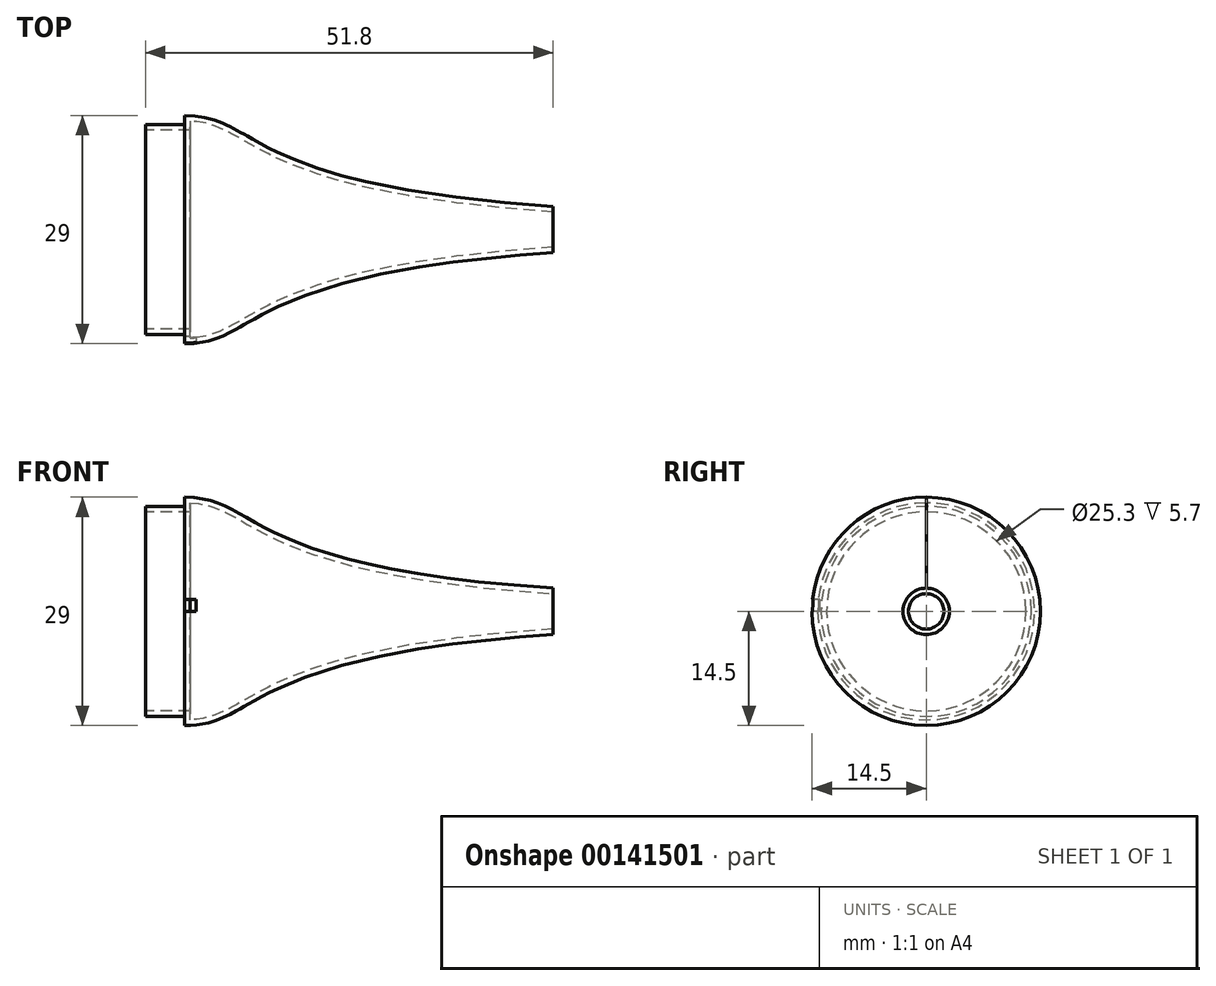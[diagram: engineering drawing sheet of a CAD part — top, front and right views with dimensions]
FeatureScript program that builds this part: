
annotation { "Feature Type Name" : "Feature", "Feature Type Description" : "" }
export const myFeature = defineFeature(function(context is Context, id is Id, definition is map)
    precondition{}
    {
        {
            var Q0;
            Q0=qCreatedBy(makeId("Front.planeOp"),FACE);
            var sketch = newSketch(context, id + "F0", { "sketchPlane" : qUnion([Q0])});
            skLineSegment(sketch, "E0", {"start": v(-28.81, 0) * mm, "end": v(31.47, 0) * mm, "construction": true});
            skLineSegment(sketch, "E1", {"start": v(0, 0) * mm, "end": v(0, 13.35) * mm});
            skLineSegment(sketch, "E2", {"start": v(0, 13.35) * mm, "end": v(5, 13.35) * mm});
            skLineSegment(sketch, "E3", {"start": v(5, 13.35) * mm, "end": v(5, 14.5) * mm});
            skLineSegment(sketch, "E4", {"start": v(51.8, 2.95) * mm, "end": v(51.8, 0) * mm});
            skLineSegment(sketch, "E5", {"start": v(51.8, 0) * mm, "end": v(0, 0) * mm});
            skFitSpline(sketch, "E6", {"points": [v(5, 14.5) * mm, v(51.8, 2.95) * mm], "startDerivative": vector(28.87, 0) * mm, "endDerivative": vector(119.6, -7.8) * mm});
            skSolve(sketch);
        }
        {
            var Q0;
            Q0 = qSketchRegion(id + "F0", true);
            var Q1;
            Q1=sQuery(id+"F0.wireOp",EDGE,"E0");
            revolve(context, id + "F1", {"entities" : qUnion([Q0]), "axis" : qUnion([Q1]), "revolveType" : RevolveType.FULL});
        }
        {
            var Q0;
            Q0=makeQuery(id+"F1.opRevolve","SWEPT_FACE",FACE,{"disambiguationData":[OSD([sQuery(id+"F0.wireOp",EDGE,"E1")])]});
            var Q1;
            Q1=makeQuery(id+"F1.opRevolve","SWEPT_FACE",FACE,{"disambiguationData":[OSD([sQuery(id+"F0.wireOp",EDGE,"E4")])]});
            shell(context, id + "F2", {"entities" : qUnion([Q0, Q1]), "thickness" : .7 * mm});
        }
        {
            var Q0;
            Q0=qCreatedBy(makeId("Front.planeOp"),FACE);
            cPlane(context, id + "F3", {"entities" : qUnion([Q0]), "cplaneType" : CPlaneType.OFFSET, "offset" : (29 / 2) * mm, "width" : 150 * mm, "height" : 150 * mm});
        }
        {
            var Q0;
            Q0=qCreatedBy(id+"F3.planeOp",FACE);
            var sketch = newSketch(context, id + "F4", { "sketchPlane" : qUnion([Q0])});
            skLineSegment(sketch, "E7.bottom", {"start": v(4.94, 1.5) * mm, "end": v(6.44, 1.5) * mm});
            skLineSegment(sketch, "E7.top", {"start": v(4.94, 0) * mm, "end": v(6.44, 0) * mm});
            skLineSegment(sketch, "E7.left", {"start": v(4.94, 1.5) * mm, "end": v(4.94, 0) * mm});
            skLineSegment(sketch, "E7.right", {"start": v(6.44, 1.5) * mm, "end": v(6.44, 0) * mm});
            skSolve(sketch);
        }
        {
            var Q0;
            Q0=makeQuery(id+"F4.imprint","IMPRINT",FACE,{"disambiguationData":[TD([[makeQuery(id+"F4.imprint","IMPRINT",EDGE,{"derivedFrom":sQuery(id+"F4.wireOp",EDGE,"E7.bottom")}),-1.0]])]});
            extrude(context, id + "F5", {"entities" : qUnion([Q0]), "operationType" : NewBodyOperationType.REMOVE, "oppositeDirection" : true, "depth" : 1 * mm});
        }
    });
